# Revit family: Somati-System_GGS_Vertical-fire-sliding-system_electric-drive_EI120
name_source: partatom
category: Doors
revit_build: Autodesk Revit 2018 (Build: 20181011_1500(x64)
units: mm (PartAtom-declared; Revit-internal decimal feet)

## family parameters
Always vertical = Yes
Cut with Voids When Loaded = No
Host = Wall
OmniClass Number = 23.30.10.00
OmniClass Title = Doors
Room Calculation Point = No
Shared = No

## types (1)
- EI 120
    Available surface fnish = Galvanized Stainless Steel PVC, MDF, HDF, laminate or veneer, STANDARD RAL 7035, 9002, 9006, 9010, and powder coating of whole RAL pallet
    BIMobject category = Fire Doors & Shutters
    BIMobject category code = doors-fire
    BIMobject main category = Doors
    BIMobject main category code = doors
    Design country = Poland
    Edition number = 1
    Engine Material = Somati - Stainless Steel
    Fire resistance = EI 60, EI 120 n
    Function = Interior
    Gate Control type = electromagnetic brake, SI engine, hydraulic drive
    Height = 3000 mm  [stored 9.84252 ft]
    Manufacturer = Somati System
    Manufacturer country = Poland
    Manufacturer name = Somati System
    Material main = Steel
    Material secondary = Composite
    Max number of opening cycles = 50000
    Model = GGS
    Nominal height = 0 mm  [stored 0 ft]
    Nominal width = 0 mm  [stored 0 ft]
    Power supply of control panel = Electromagnetic brake:1 x 230V/50Hz/6A, SI : 1x230V/50HZ/20A, Hydraulic: 3x 400V/50 HZ/16A
    Product Guid = 5bca31b6-f156-4a66-a39c-9698f8e5fb81
    Product SKU = GGS_VERTICAL_FIRE_SLIDING_DOOR
    Product data url = https://bimobject.com
    Product family = GGS
    Product group = GGS
    Product url = https://somati-system.pl
    QR code = http://bimobject.com
    Technical description = https://somati-system.pl
    Thickness = 0 mm  [stored 0 ft]
    Wall Closure = By host
    Weight Net (Kg) = 0
    Width = 2500 mm  [stored 8.2021 ft]
    Wing thickness = 81 mm
    Youtube clip = https://www.youtube.com

note: [stored X ft] marks values corroborated as IEEE doubles in the binary element streams (Revit-internal decimal feet)

## geometry (parser evidence)
native form markers: Sweep x18
no freeform markers — native parametric forms only
